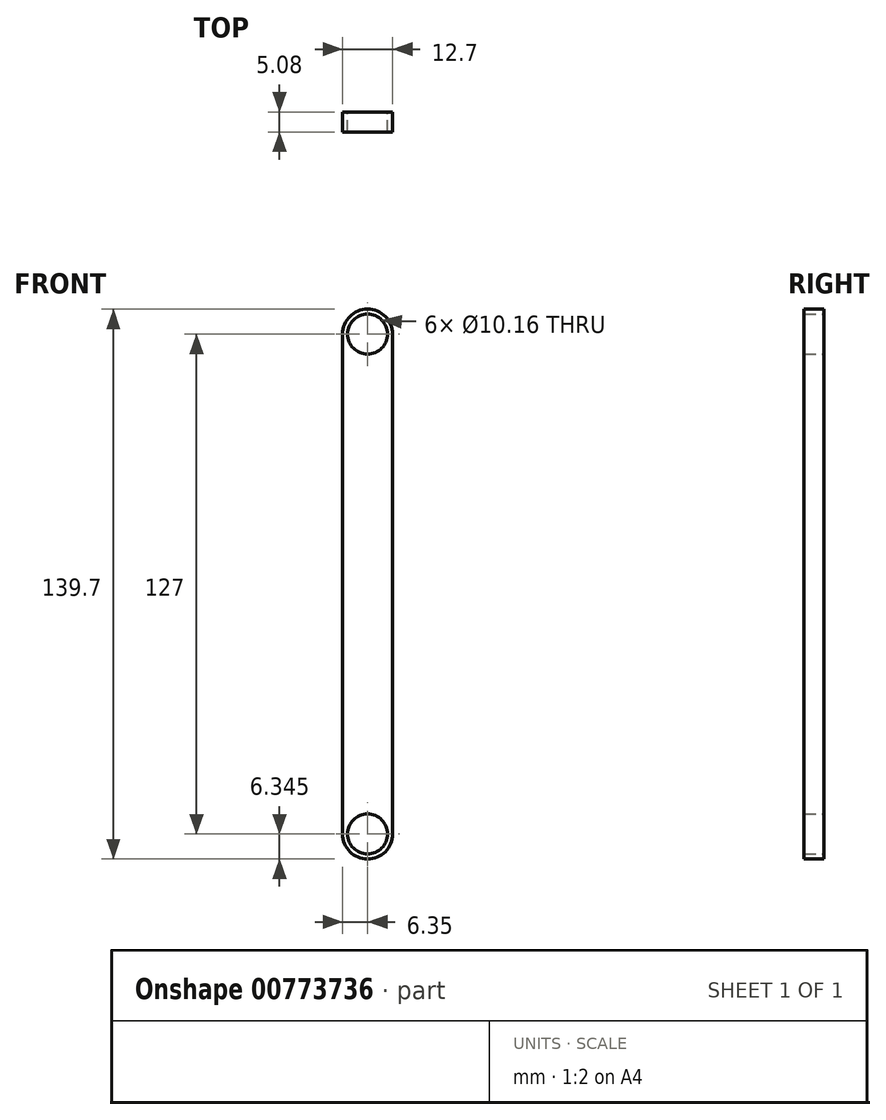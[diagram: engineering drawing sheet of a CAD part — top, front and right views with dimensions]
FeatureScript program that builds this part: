
annotation { "Feature Type Name" : "Feature", "Feature Type Description" : "" }
export const myFeature = defineFeature(function(context is Context, id is Id, definition is map)
    precondition{}
    {
        {
            var Q0;
            Q0=qCreatedBy(makeId("Front.planeOp"),FACE);
            var sketch = newSketch(context, id + "F0", { "sketchPlane" : qUnion([Q0])});
            skCircle(sketch, "E0", {"center": v(0, 80.36) * mm, "radius": 5.08 * mm});
            skCircle(sketch, "E1", {"center": v(0, 80.36) * mm, "radius": 6.35 * mm});
            skCircle(sketch, "E2", {"center": v(0, -46.64) * mm, "radius": 5.08 * mm});
            skCircle(sketch, "E3", {"center": v(0, -46.64) * mm, "radius": 6.35 * mm});
            skLineSegment(sketch, "E4", {"start": v(0, 80.36) * mm, "end": v(0, -46.64) * mm, "construction": true});
            skLineSegment(sketch, "E5", {"start": v(-6.35, 80.36) * mm, "end": v(-6.35, -46.64) * mm});
            skLineSegment(sketch, "E6", {"start": v(6.35, 80.36) * mm, "end": v(6.35, -46.64) * mm});
            skSolve(sketch);
        }
        {
            var Q0;
            {var subQ0=sQuery(id+"F0.wireOp",EDGE,"E5");Q0=makeQuery(id+"F0.imprint","IMPRINT",FACE,{"disambiguationData":[TD([[makeQuery(id+"F0.imprint","IMPRINT",EDGE,{"derivedFrom":subQ0}),1.0]])]});}
            var Q1;
            Q1=makeQuery(id+"F0.imprint","IMPRINT",FACE,{"disambiguationData":[TD([[makeQuery(id+"F0.imprint","IMPRINT",EDGE,{"derivedFrom":sQuery(id+"F0.wireOp",EDGE,"E0")}),-1.0]])]});
            var Q2;
            Q2=makeQuery(id+"F0.imprint","IMPRINT",FACE,{"disambiguationData":[TD([[makeQuery(id+"F0.imprint","IMPRINT",EDGE,{"derivedFrom":sQuery(id+"F0.wireOp",EDGE,"E2")}),-1.0]])]});
            extrude(context, id + "F1", {"entities" : qUnion([Q0, Q1, Q2]), "depth" : 5.08 * mm, "offsetDistance" : 25.4 * mm});
        }
    });
